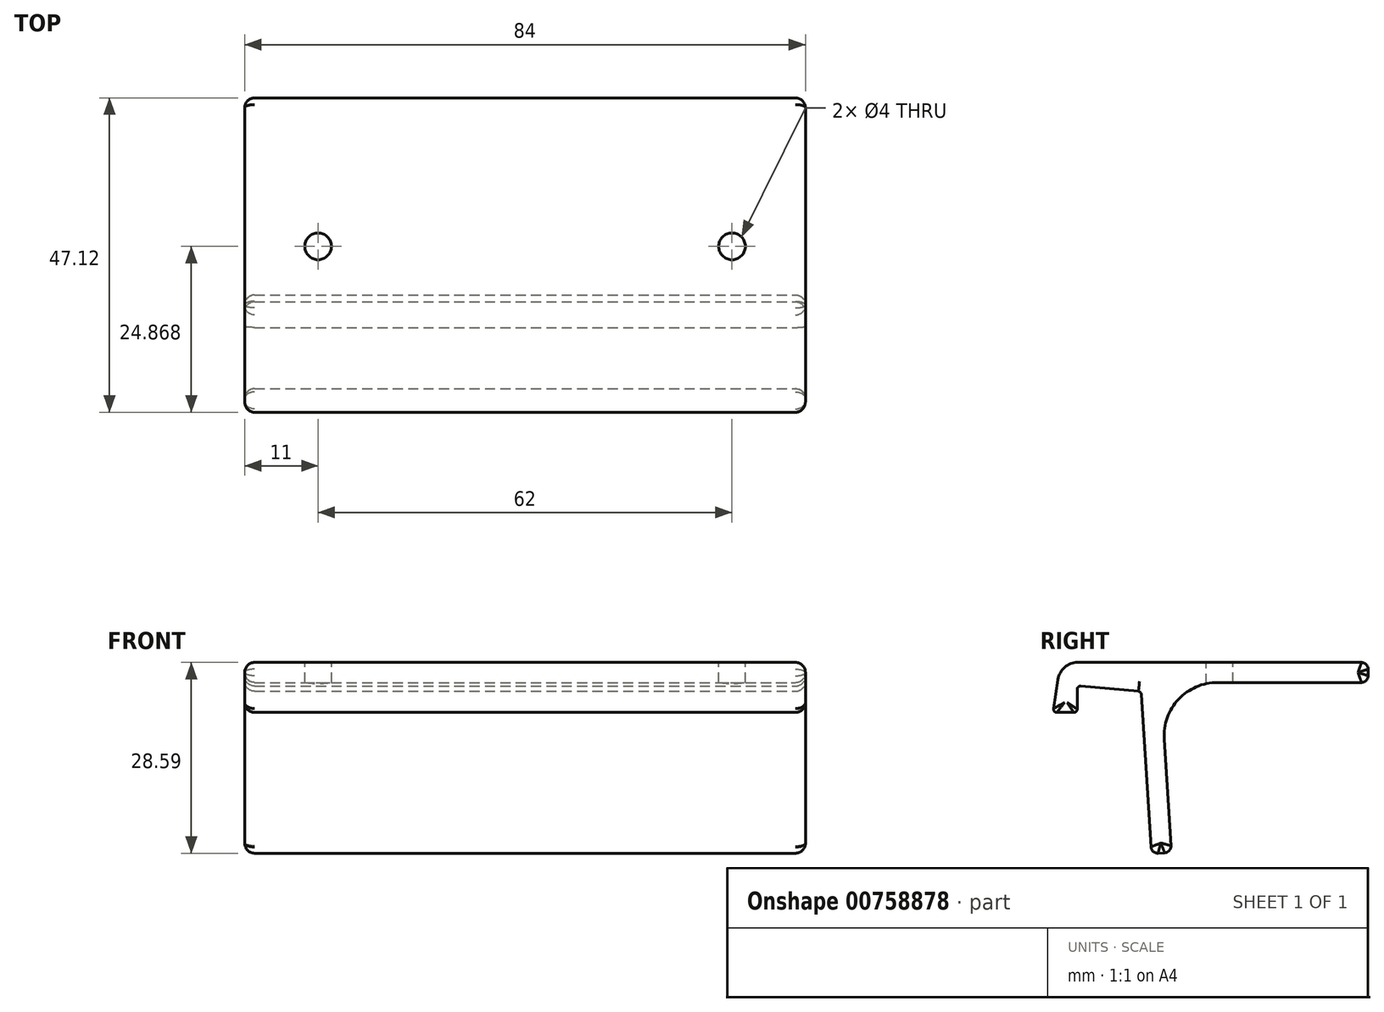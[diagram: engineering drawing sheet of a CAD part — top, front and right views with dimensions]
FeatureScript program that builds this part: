
annotation { "Feature Type Name" : "Feature", "Feature Type Description" : "" }
export const myFeature = defineFeature(function(context is Context, id is Id, definition is map)
    precondition{}
    {
        {
            var Q0;
            Q0=qCreatedBy(makeId("Right.planeOp"),FACE);
            var sketch = newSketch(context, id + "F0", { "sketchPlane" : qUnion([Q0])});
            skLineSegment(sketch, "E0", {"start": v(4.13, -24.24) * mm, "end": v(3.13, -24.3) * mm});
            skPoint(sketch, "E1.visualSharp", {"position": v(-11.43, 4.74) * mm});
            skArc(sketch, "E1.filletArc", {"start": v(-8.9, 4.3) * mm, "mid": v(-10.86, 3.57) * mm, "end": v(-11.87, 1.74) * mm});
            skPoint(sketch, "E2.visualSharp", {"position": v(-12.52, -2.62) * mm});
            skPoint(sketch, "E3.visualSharp", {"position": v(2.14, -24.36) * mm});
            skArc(sketch, "E3.filletArc", {"start": v(2.07, -23.36) * mm, "mid": v(2.4, -24.05) * mm, "end": v(3.13, -24.3) * mm});
            skPoint(sketch, "E4.visualSharp", {"position": v(5.13, -24.17) * mm});
            skArc(sketch, "E4.filletArc", {"start": v(4.13, -24.24) * mm, "mid": v(4.82, -23.9) * mm, "end": v(5.07, -23.17) * mm});
            skLineSegment(sketch, "E5", {"start": v(2.07, -23.36) * mm, "end": v(0.62, -0.5) * mm});
            skPoint(sketch, "E6.visualSharp", {"position": v(0.6, -0.09) * mm});
            skArc(sketch, "E6.filletArc", {"start": v(0.62, -0.5) * mm, "mid": v(0.49, -0.19) * mm, "end": v(0.2, -0.03) * mm});
            skPoint(sketch, "E7.visualSharp", {"position": v(-8.9, 1.33) * mm});
            skLineSegment(sketch, "E8", {"start": v(-8.9, 4.3) * mm, "end": v(33.6, 4.3) * mm});
            skLineSegment(sketch, "E9", {"start": v(5.07, -23.17) * mm, "end": v(4.05, -7.21) * mm});
            skLineSegment(sketch, "E10.0", {"start": v(12.04, 1.3) * mm, "end": v(33.6, 1.3) * mm});
            skLineSegment(sketch, "E11", {"start": v(34.6, 2.3) * mm, "end": v(34.6, 3.3) * mm});
            skPoint(sketch, "E12.visualSharp", {"position": v(3.51, 1.3) * mm});
            skArc(sketch, "E12.filletArc", {"start": v(12.04, 1.3) * mm, "mid": v(6.2, -1.23) * mm, "end": v(4.05, -7.21) * mm});
            skPoint(sketch, "E13.visualSharp", {"position": v(34.6, 1.3) * mm});
            skArc(sketch, "E13.filletArc", {"start": v(33.6, 1.3) * mm, "mid": v(34.3, 1.59) * mm, "end": v(34.6, 2.3) * mm});
            skPoint(sketch, "E14.visualSharp", {"position": v(34.6, 4.3) * mm});
            skArc(sketch, "E14.filletArc", {"start": v(34.6, 3.3) * mm, "mid": v(34.3, 4) * mm, "end": v(33.6, 4.3) * mm});
            skLineSegment(sketch, "E15", {"start": v(0.2, -0.03) * mm, "end": v(-8.43, 0.75) * mm});
            skLineSegment(sketch, "E16", {"start": v(-8.98, 0.25) * mm, "end": v(-8.98, -2.7) * mm});
            skLineSegment(sketch, "E17", {"start": v(-11.87, 1.74) * mm, "end": v(-12.52, -2.63) * mm});
            skLineSegment(sketch, "E18", {"start": v(-9.48, -3.2) * mm, "end": v(-12.02, -3.2) * mm});
            skPoint(sketch, "E19.visualSharp", {"position": v(-8.98, 0.8) * mm});
            skArc(sketch, "E19.filletArc", {"start": v(-8.43, 0.75) * mm, "mid": v(-8.81, 0.62) * mm, "end": v(-8.98, 0.25) * mm});
            skPoint(sketch, "E20.visualSharp", {"position": v(-12.6, -3.2) * mm});
            skArc(sketch, "E20.filletArc", {"start": v(-12.52, -2.63) * mm, "mid": v(-12.4, -3.03) * mm, "end": v(-12.02, -3.2) * mm});
            skPoint(sketch, "E21.visualSharp", {"position": v(-8.98, -3.2) * mm});
            skArc(sketch, "E21.filletArc", {"start": v(-9.48, -3.2) * mm, "mid": v(-9.12, -3.05) * mm, "end": v(-8.98, -2.7) * mm});
            skSolve(sketch);
        }
        {
            var Q0;
            Q0=makeQuery(id+"F0.imprint","IMPRINT",FACE,{"disambiguationData":[TD([[makeQuery(id+"F0.imprint","IMPRINT",EDGE,{"derivedFrom":sQuery(id+"F0.wireOp",EDGE,"E0")}),-1.0]])]});
            extrude(context, id + "F1", {"entities" : qUnion([Q0]), "oppositeDirection" : true, "depth" : 84 * mm, "offsetDistance" : 25 * mm});
        }
        {
            var Q0;
            Q0=makeQuery(id+"F1.opExtrude","CAP_EDGE",EDGE,{"disambiguationData":[OSD([sQuery(id+"F0.wireOp",EDGE,"E8")])],"isStart":true});
            var Q1;
            Q1=makeQuery(id+"F1.opExtrude","CAP_EDGE",EDGE,{"disambiguationData":[OSD([sQuery(id+"F0.wireOp",EDGE,"E8")])],"isStart":false});
            fillet(context, id + "F2", {"entities" : qUnion([Q0, Q1]), "radius" : 1.5 * mm, "tangentPropagation" : true, "allowEdgeOverflow" : false});
        }
        {
            var Q0;
            Q0=makeQuery(id+"F1.opExtrude","SWEPT_FACE",FACE,{"disambiguationData":[OSD([sQuery(id+"F0.wireOp",EDGE,"E8")])]});
            var sketch = newSketch(context, id + "F3", { "sketchPlane" : qUnion([Q0])});
            skLineSegment(sketch, "E22.0.0", {"start": v(-82.5, -8.9) * mm, "end": v(-1.5, -8.9) * mm, "construction": true});
            skLineSegment(sketch, "E22.0.1", {"start": v(-1.5, -8.9) * mm, "end": v(-1.5, 33.6) * mm, "construction": true});
            skLineSegment(sketch, "E22.0.2", {"start": v(-1.5, 33.6) * mm, "end": v(-82.5, 33.6) * mm, "construction": true});
            skLineSegment(sketch, "E22.0.3", {"start": v(-82.5, 33.6) * mm, "end": v(-82.5, -8.9) * mm, "construction": true});
            skLineSegment(sketch, "E23", {"start": v(-82.5, 12.35) * mm, "end": v(-73, 12.35) * mm, "construction": true});
            skLineSegment(sketch, "E24", {"start": v(-1.5, 12.35) * mm, "end": v(-11, 12.35) * mm, "construction": true});
            skCircle(sketch, "E25", {"center": v(-73, 12.35) * mm, "radius": 2 * mm});
            skCircle(sketch, "E26", {"center": v(-11, 12.35) * mm, "radius": 2 * mm});
            skSolve(sketch);
        }
        {
            var Q0;
            Q0 = qSketchRegion(id + "F3", true);
            extrude(context, id + "F4", {"entities" : qUnion([Q0]), "operationType" : NewBodyOperationType.REMOVE, "oppositeDirection" : true, "depth" : 25 * mm, "offsetDistance" : 25 * mm});
        }
    });
